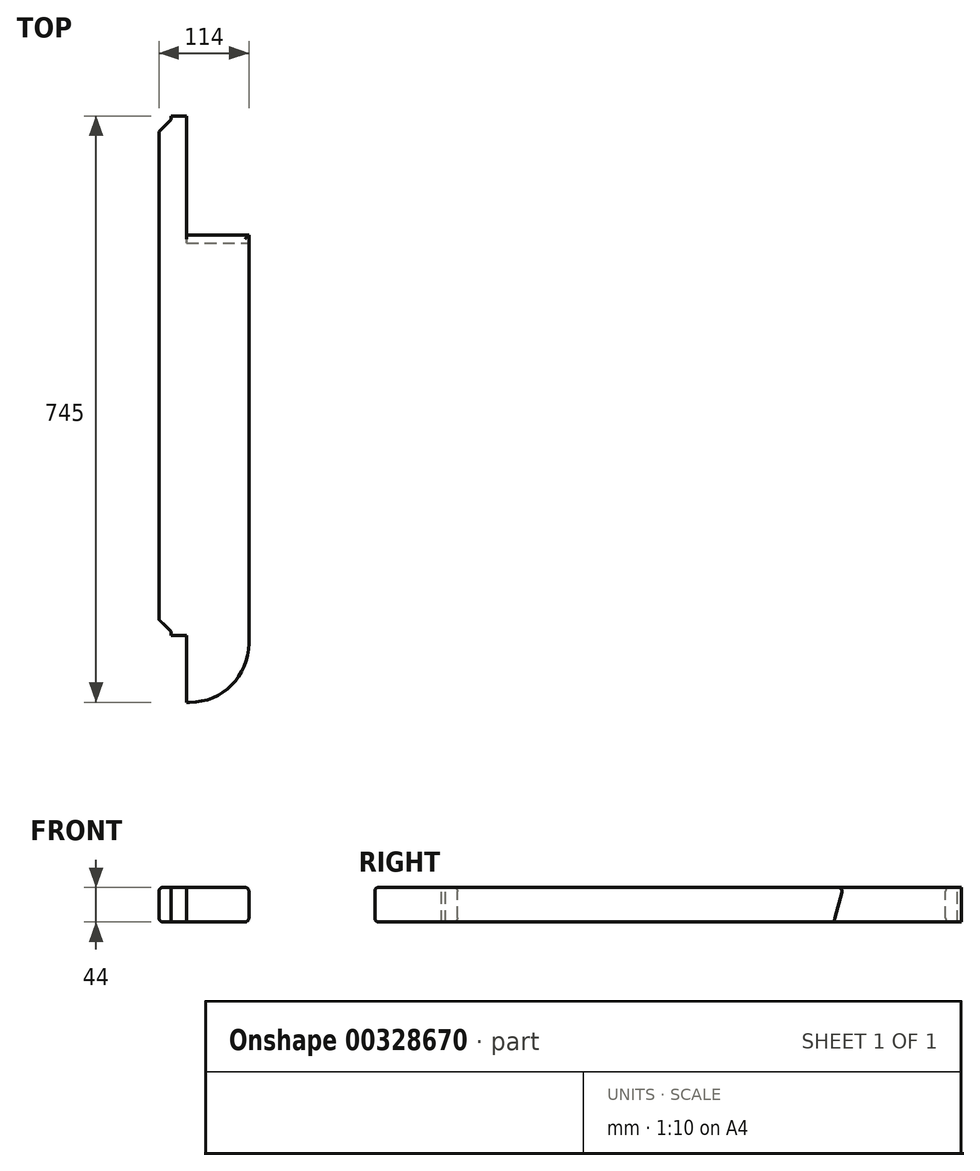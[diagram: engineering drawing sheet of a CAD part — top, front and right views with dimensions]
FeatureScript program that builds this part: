
annotation { "Feature Type Name" : "Feature", "Feature Type Description" : "" }
export const myFeature = defineFeature(function(context is Context, id is Id, definition is map)
    precondition{}
    {
        {
            var Q0;
            Q0=qCreatedBy(makeId("Top.planeOp"),FACE);
            var sketch = newSketch(context, id + "F0", { "sketchPlane" : qUnion([Q0])});
            skLineSegment(sketch, "E0.bottom", {"start": v(35, 0) * mm, "end": v(39, 0) * mm});
            skLineSegment(sketch, "E0.top", {"start": v(15, 745) * mm, "end": v(35, 745) * mm});
            skLineSegment(sketch, "E0.left", {"start": v(0, 105) * mm, "end": v(0, 725) * mm});
            skLineSegment(sketch, "E0.right", {"start": v(114, 75) * mm, "end": v(114, 595) * mm});
            skLineSegment(sketch, "E1", {"start": v(35, 0) * mm, "end": v(35, 85) * mm});
            skLineSegment(sketch, "E2", {"start": v(35, 85) * mm, "end": v(15, 85) * mm});
            skLineSegment(sketch, "E3", {"start": v(0, 0) * mm, "end": v(35, 0) * mm, "construction": true});
            skLineSegment(sketch, "E4", {"start": v(0, 0) * mm, "end": v(0, 85) * mm, "construction": true});
            skPoint(sketch, "E5.visualSharp", {"position": v(114, 0) * mm});
            skArc(sketch, "E5.filletArc", {"start": v(39, 0) * mm, "mid": v(92.03, 21.97) * mm, "end": v(114, 75) * mm});
            skLineSegment(sketch, "E6", {"start": v(0, 105) * mm, "end": v(15, 90) * mm});
            skLineSegment(sketch, "E7", {"start": v(15, 90) * mm, "end": v(15, 85) * mm});
            skLineSegment(sketch, "E8", {"start": v(114, 595) * mm, "end": v(35, 595) * mm});
            skLineSegment(sketch, "E9", {"start": v(35, 595) * mm, "end": v(35, 745) * mm});
            skLineSegment(sketch, "E10", {"start": v(0, 725) * mm, "end": v(15, 740) * mm});
            skLineSegment(sketch, "E11", {"start": v(15, 740) * mm, "end": v(15, 745) * mm});
            skPoint(sketch, "E12.orphan", {"position": v(0, 745) * mm});
            skSolve(sketch);
        }
        {
            var Q0;
            Q0=makeQuery(id+"F0.imprint","IMPRINT",FACE,{"disambiguationData":[TD([[makeQuery(id+"F0.imprint","IMPRINT",EDGE,{"derivedFrom":sQuery(id+"F0.wireOp",EDGE,"E0.bottom")}),1.0]])]});
            extrude(context, id + "F1", {"entities" : qUnion([Q0]), "oppositeDirection" : true, "depth" : 44 * mm});
        }
        {
            var Q0;
            Q0=makeQuery(id+"F1.opExtrude","SWEPT_FACE",FACE,{"disambiguationData":[OSD([sQuery(id+"F0.wireOp",EDGE,"E0.right")])]});
            var sketch = newSketch(context, id + "F2", { "sketchPlane" : qUnion([Q0])});
            skLineSegment(sketch, "E13", {"start": v(595, 0) * mm, "end": v(583.21, -44) * mm});
            skLineSegment(sketch, "E14", {"start": v(583.21, -44) * mm, "end": v(595, -44) * mm});
            skLineSegment(sketch, "E15", {"start": v(595, -44) * mm, "end": v(595, 0) * mm});
            skSolve(sketch);
        }
        {
            var Q0;
            Q0=qSketchRegion(id+"F2",true);
            extrude(context, id + "F3", {"entities" : qUnion([Q0]), "operationType" : NewBodyOperationType.REMOVE, "oppositeDirection" : true, "depth" : 79 * mm});
        }
        {
            var Q0;
            Q0=makeQuery(id+"F1.opExtrude","CAP_EDGE",EDGE,{"disambiguationData":[OSD([sQuery(id+"F0.wireOp",EDGE,"E0.bottom")])],"isStart":true});
            var Q1;
            Q1=makeQuery(id+"F1.opExtrude","CAP_EDGE",EDGE,{"disambiguationData":[OSD([sQuery(id+"F0.wireOp",EDGE,"E0.right")])],"isStart":false});
            var Q2;
            Q2=makeQuery(id+"F1.opExtrude","CAP_EDGE",EDGE,{"disambiguationData":[OSD([sQuery(id+"F0.wireOp",EDGE,"E0.left")])],"isStart":true});
            var Q3;
            Q3=makeQuery(id+"F1.opExtrude","CAP_EDGE",EDGE,{"disambiguationData":[OSD([sQuery(id+"F0.wireOp",EDGE,"E0.left")])],"isStart":false});
            var Q4;
            Q4=makeQuery(id+"F3.boolean.opBoolean","MERGE",EDGE,{"derivedFrom":[makeQuery(id+"F1.opExtrude","CAP_EDGE",EDGE,{"disambiguationData":[OSD([sQuery(id+"F0.wireOp",EDGE,"E8")])],"isStart":true}),makeQuery(id+"F3.opExtrude","SWEPT_EDGE",EDGE,{"disambiguationData":[OSD([sQuery(id+"F0.wireOp",EDGE,"E0.right"),sQuery(id+"F2.wireOp",EDGE,"E13"),sQuery(id+"F2.wireOp",EDGE,"E15")])]})]});
            fillet(context, id + "F4", {"entities" : qUnion([Q0, Q1, Q2, Q3, Q4]), "radius" : 5 * mm, "tangentPropagation" : true, "allowEdgeOverflow" : false});
        }
    });
